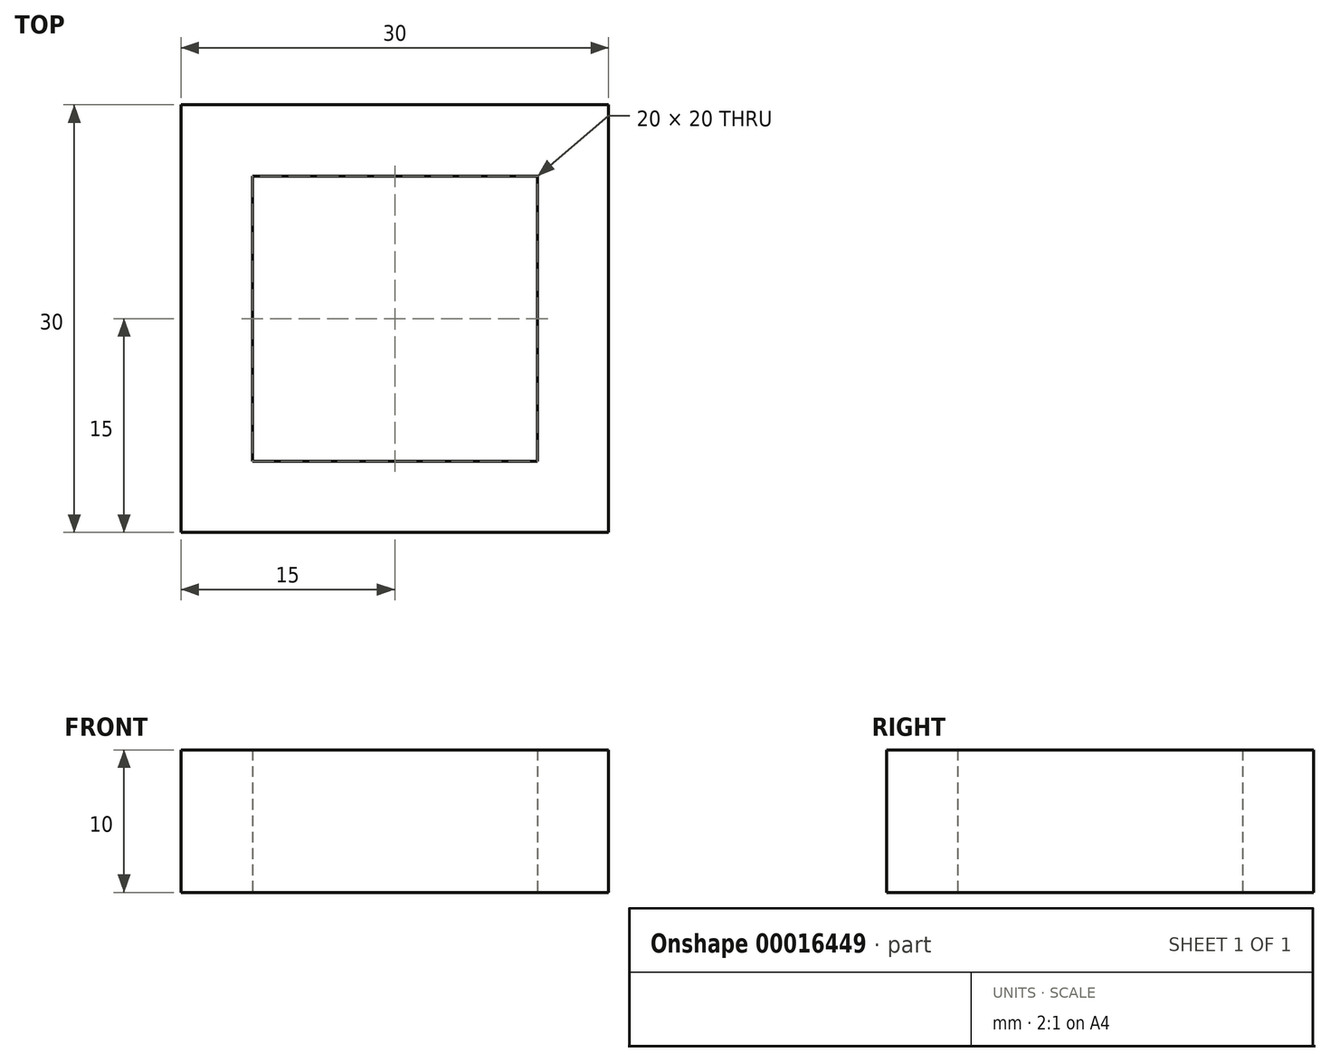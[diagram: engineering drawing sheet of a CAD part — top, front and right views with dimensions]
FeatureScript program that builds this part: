
annotation { "Feature Type Name" : "Feature", "Feature Type Description" : "" }
export const myFeature = defineFeature(function(context is Context, id is Id, definition is map)
    precondition{}
    {
        {
            var Q0;
            Q0=qCreatedBy(makeId("Top.planeOp"),FACE);
            var sketch = newSketch(context, id + "F0", { "sketchPlane" : qUnion([Q0])});
            skLineSegment(sketch, "E0.bottom", {"start": v(15, -15) * mm, "end": v(-15, -15) * mm});
            skLineSegment(sketch, "E0.top", {"start": v(15, 15) * mm, "end": v(-15, 15) * mm});
            skLineSegment(sketch, "E0.left", {"start": v(15, -15) * mm, "end": v(15, 15) * mm});
            skLineSegment(sketch, "E0.right", {"start": v(-15, -15) * mm, "end": v(-15, 15) * mm});
            skPoint(sketch, "E0.middle", {"position": v(0, 0) * mm});
            skLineSegment(sketch, "E1.0", {"start": v(10, -10) * mm, "end": v(-10, -10) * mm});
            skLineSegment(sketch, "E1.1", {"start": v(10, -10) * mm, "end": v(10, 10) * mm});
            skLineSegment(sketch, "E1.2", {"start": v(10, 10) * mm, "end": v(-10, 10) * mm});
            skLineSegment(sketch, "E1.3", {"start": v(-10, -10) * mm, "end": v(-10, 10) * mm});
            skSolve(sketch);
        }
        {
            var Q0;
            Q0=makeQuery(id+"F0.imprint","IMPRINT",FACE,{"disambiguationData":[TD([[makeQuery(id+"F0.imprint","IMPRINT",EDGE,{"derivedFrom":sQuery(id+"F0.wireOp",EDGE,"E0.bottom")}),-1.0]])]});
            extrude(context, id + "F1", {"entities" : qUnion([Q0]), "depth" : 10 * mm});
        }
    });
